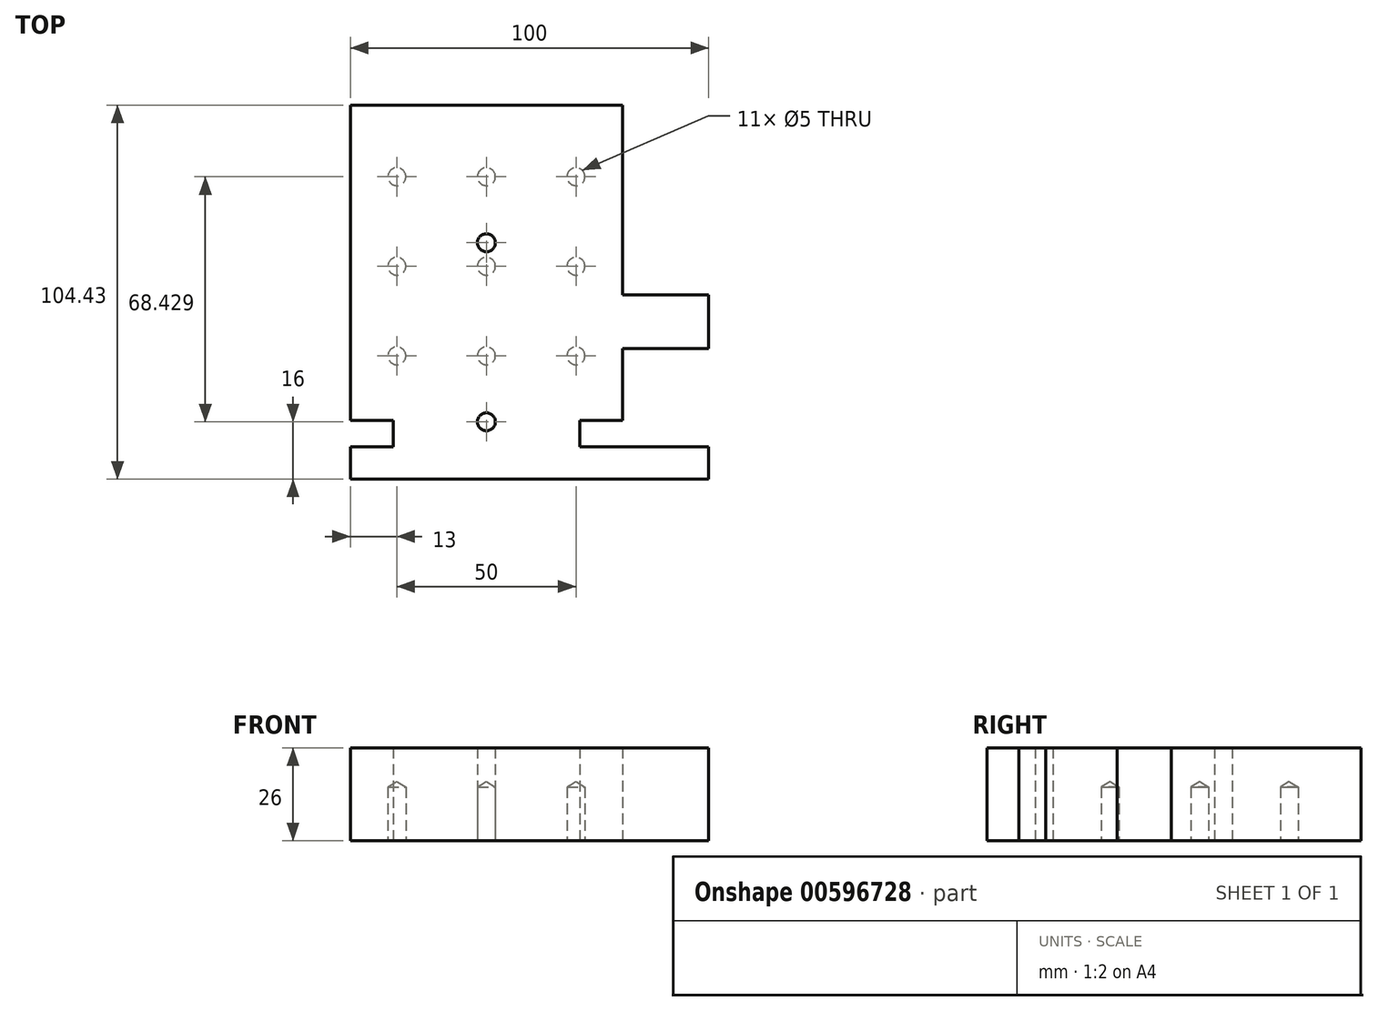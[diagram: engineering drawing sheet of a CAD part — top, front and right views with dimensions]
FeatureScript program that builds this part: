
annotation { "Feature Type Name" : "Feature", "Feature Type Description" : "" }
export const myFeature = defineFeature(function(context is Context, id is Id, definition is map)
    precondition{}
    {
        {
            var Q0;
            Q0=qCreatedBy(makeId("Top.planeOp"),FACE);
            var sketch = newSketch(context, id + "F0", { "sketchPlane" : qUnion([Q0])});
            skLineSegment(sketch, "E0", {"start": v(62, -9) * mm, "end": v(-38, -9) * mm});
            skLineSegment(sketch, "E1", {"start": v(-38, -9) * mm, "end": v(-38, 0) * mm});
            skLineSegment(sketch, "E2", {"start": v(-38, 0) * mm, "end": v(-26, 0) * mm});
            skLineSegment(sketch, "E3", {"start": v(-26, 0) * mm, "end": v(-26, 7.43) * mm});
            skLineSegment(sketch, "E4", {"start": v(-26, 7.43) * mm, "end": v(-38, 7.43) * mm});
            skLineSegment(sketch, "E5", {"start": v(-38, 7.43) * mm, "end": v(-38, 95.43) * mm});
            skLineSegment(sketch, "E6", {"start": v(-38, 95.43) * mm, "end": v(38, 95.43) * mm});
            skLineSegment(sketch, "E7", {"start": v(38, 95.43) * mm, "end": v(38, 42.43) * mm});
            skLineSegment(sketch, "E8", {"start": v(38, 42.43) * mm, "end": v(62, 42.43) * mm});
            skLineSegment(sketch, "E9", {"start": v(62, 42.43) * mm, "end": v(62, 27.43) * mm});
            skLineSegment(sketch, "E10", {"start": v(62, 27.43) * mm, "end": v(38, 27.43) * mm});
            skLineSegment(sketch, "E11", {"start": v(38, 27.43) * mm, "end": v(38, 7.43) * mm});
            skLineSegment(sketch, "E12", {"start": v(38, 7.43) * mm, "end": v(26, 7.43) * mm});
            skLineSegment(sketch, "E13", {"start": v(26, 7.43) * mm, "end": v(26, 0) * mm});
            skLineSegment(sketch, "E14", {"start": v(26, 0) * mm, "end": v(62, 0) * mm});
            skLineSegment(sketch, "E15", {"start": v(62, -9) * mm, "end": v(62, 0) * mm});
            skCircle(sketch, "E16", {"center": v(0, 7) * mm, "radius": 2.5 * mm});
            skCircle(sketch, "E17", {"center": v(0, 57) * mm, "radius": 2.5 * mm});
            skSolve(sketch);
        }
        {
            var Q0;
            Q0 = qSketchRegion(id + "F0", true);
            extrude(context, id + "F1", {"entities" : qUnion([Q0]), "depth" : 26 * mm, "offsetDistance" : 25 * mm});
        }
        {
            var Q0;
            Q0=makeQuery(id+"F1.opExtrude","CAP_FACE",FACE,{"disambiguationData":[OSD([sQuery(id+"F0.wireOp",EDGE,"E0"),sQuery(id+"F0.wireOp",EDGE,"E1"),sQuery(id+"F0.wireOp",EDGE,"E2"),sQuery(id+"F0.wireOp",EDGE,"E3"),sQuery(id+"F0.wireOp",EDGE,"E4"),sQuery(id+"F0.wireOp",EDGE,"E5"),sQuery(id+"F0.wireOp",EDGE,"E6"),sQuery(id+"F0.wireOp",EDGE,"E7"),sQuery(id+"F0.wireOp",EDGE,"E8"),sQuery(id+"F0.wireOp",EDGE,"E9"),sQuery(id+"F0.wireOp",EDGE,"E10"),sQuery(id+"F0.wireOp",EDGE,"E11"),sQuery(id+"F0.wireOp",EDGE,"E12"),sQuery(id+"F0.wireOp",EDGE,"E13"),sQuery(id+"F0.wireOp",EDGE,"E14"),sQuery(id+"F0.wireOp",EDGE,"E15"),sQuery(id+"F0.wireOp",EDGE,"E16"),sQuery(id+"F0.wireOp",EDGE,"E17")])],"isStart":true});
            var sketch = newSketch(context, id + "F2", { "sketchPlane" : qUnion([Q0])});
            skPoint(sketch, "E18", {"position": v(-25, -75.43) * mm});
            skPoint(sketch, "E19.0.1.0", {"position": v(-25, -50.43) * mm});
            skPoint(sketch, "E19.0.2.0", {"position": v(-25, -25.43) * mm});
            skPoint(sketch, "E19.1.0.0", {"position": v(0, -75.43) * mm});
            skPoint(sketch, "E19.1.1.0", {"position": v(0, -50.43) * mm});
            skPoint(sketch, "E19.1.2.0", {"position": v(0, -25.43) * mm});
            skPoint(sketch, "E19.2.0.0", {"position": v(25, -75.43) * mm});
            skPoint(sketch, "E19.2.1.0", {"position": v(25, -50.43) * mm});
            skPoint(sketch, "E19.2.2.0", {"position": v(25, -25.43) * mm});
            skLineSegment(sketch, "E19.direction1", {"start": v(-25, -75.43) * mm, "end": v(0, -75.43) * mm, "construction": true});
            skLineSegment(sketch, "E19.direction2", {"start": v(-25, -75.43) * mm, "end": v(-25, -50.43) * mm, "construction": true});
            skSolve(sketch);
        }
        {
            var Q0;
            Q0=sQuery(id+"F2.wireOp",VERTEX,"E19.0.2.0");
            var Q1;
            Q1=sQuery(id+"F2.wireOp",VERTEX,"E19.1.0.0");
            var Q2;
            Q2=sQuery(id+"F2.wireOp",VERTEX,"E18");
            var Q3;
            Q3=sQuery(id+"F2.wireOp",VERTEX,"E19.0.1.0");
            var Q4;
            Q4=sQuery(id+"F2.wireOp",VERTEX,"E19.2.1.0");
            var Q5;
            Q5=sQuery(id+"F2.wireOp",VERTEX,"E19.1.1.0");
            var Q6;
            Q6=sQuery(id+"F2.wireOp",VERTEX,"E19.2.0.0");
            var Q7;
            Q7=sQuery(id+"F2.wireOp",VERTEX,"E19.1.2.0");
            var Q8;
            Q8=sQuery(id+"F2.wireOp",VERTEX,"E19.2.2.0");
            var Q9;
            Q9=makeQuery(id+"F1.opExtrude","SWEPT_BODY",BODY,{"disambiguationData":[OSD([sQuery(id+"F0.wireOp",EDGE,"E0"),sQuery(id+"F0.wireOp",EDGE,"E1"),sQuery(id+"F0.wireOp",EDGE,"E2"),sQuery(id+"F0.wireOp",EDGE,"E3"),sQuery(id+"F0.wireOp",EDGE,"E4"),sQuery(id+"F0.wireOp",EDGE,"E5"),sQuery(id+"F0.wireOp",EDGE,"E6"),sQuery(id+"F0.wireOp",EDGE,"E7"),sQuery(id+"F0.wireOp",EDGE,"E8"),sQuery(id+"F0.wireOp",EDGE,"E9"),sQuery(id+"F0.wireOp",EDGE,"E10"),sQuery(id+"F0.wireOp",EDGE,"E11"),sQuery(id+"F0.wireOp",EDGE,"E12"),sQuery(id+"F0.wireOp",EDGE,"E13"),sQuery(id+"F0.wireOp",EDGE,"E14"),sQuery(id+"F0.wireOp",EDGE,"E15"),sQuery(id+"F0.wireOp",EDGE,"E16"),sQuery(id+"F0.wireOp",EDGE,"E17")])]});
            hole(context, id + "F3", {"style" : HoleStyle.SIMPLE, "endStyle" : HoleEndStyle.BLIND, "standardTappedOrClearance" : lookupTablePath({ "standard" : "ISO", "engagement" : "75%", "pitch" : "1 mm", "size" : "M6", "type" : "Tapped" }), "standardBlindInLast" : lookupTablePath({ "standard" : "ISO", "engagement" : "75%", "pitch" : "1 mm", "size" : "M6", "type" : "Tapped" }), "holeDiameter" : 5 * mm, "majorDiameter" : 6 * mm, "showTappedDepth" : true, "holeDepth" : 15 * mm, "isTappedThrough" : true, "tappedDepth" : 12 * mm, "tapClearance" : 3, "locations" : qUnion([Q0, Q1, Q2, Q3, Q4, Q5, Q6, Q7, Q8]), "scope" : qUnion([Q9])});
        }
    });
